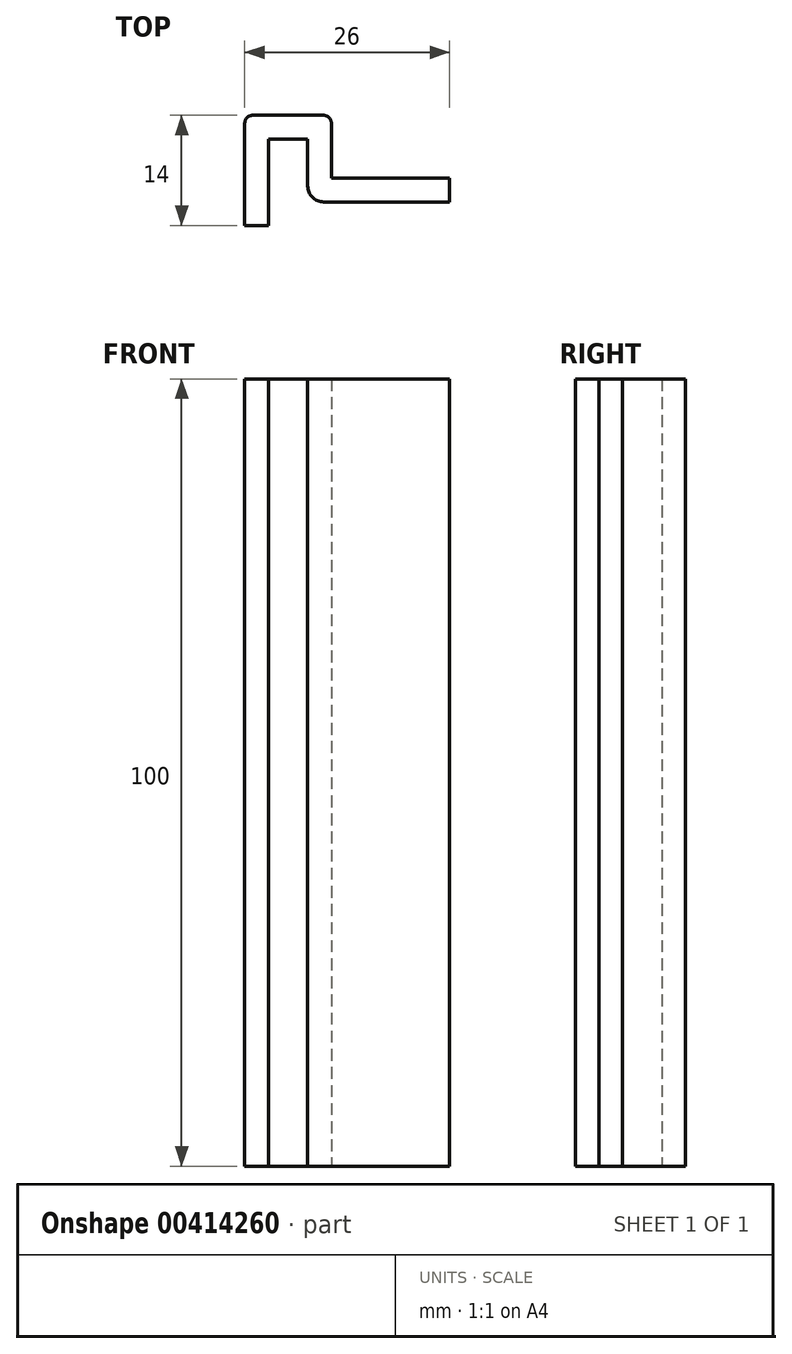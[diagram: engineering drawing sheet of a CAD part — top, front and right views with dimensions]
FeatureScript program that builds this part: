
annotation { "Feature Type Name" : "Feature", "Feature Type Description" : "" }
export const myFeature = defineFeature(function(context is Context, id is Id, definition is map)
    precondition{}
    {
        {
            var Q0;
            Q0=qCreatedBy(makeId("Top.planeOp"),FACE);
            var sketch = newSketch(context, id + "F0", { "sketchPlane" : qUnion([Q0])});
            skLineSegment(sketch, "E0", {"start": v(0, 0) * mm, "end": v(0, 14) * mm});
            skLineSegment(sketch, "E1", {"start": v(0, 14) * mm, "end": v(11, 14) * mm});
            skLineSegment(sketch, "E2", {"start": v(11, 14) * mm, "end": v(11, 6) * mm});
            skLineSegment(sketch, "E3", {"start": v(11, 6) * mm, "end": v(26, 6) * mm});
            skLineSegment(sketch, "E4", {"start": v(26, 6) * mm, "end": v(26, 3) * mm});
            skLineSegment(sketch, "E5", {"start": v(26, 3) * mm, "end": v(8, 3) * mm});
            skLineSegment(sketch, "E6", {"start": v(8, 3) * mm, "end": v(8, 11) * mm});
            skLineSegment(sketch, "E7", {"start": v(8, 11) * mm, "end": v(3, 11) * mm});
            skLineSegment(sketch, "E8", {"start": v(3, 11) * mm, "end": v(3, 0) * mm});
            skLineSegment(sketch, "E9", {"start": v(3, 0) * mm, "end": v(0, 0) * mm});
            skSolve(sketch);
        }
        {
            var Q0;
            Q0=qSketchRegion(id+"F0",true);
            extrude(context, id + "F1", {"entities" : qUnion([Q0]), "depth" : 100 * mm});
        }
        {
            var Q0;
            Q0=makeQuery(id+"F1.opExtrude","SWEPT_EDGE",EDGE,{"disambiguationData":[OSD([sQuery(id+"F0.wireOp",EDGE,"E5"),sQuery(id+"F0.wireOp",EDGE,"E6")])]});
            fillet(context, id + "F2", {"entities" : qUnion([Q0]), "radius" : 2 * mm, "tangentPropagation" : true, "allowEdgeOverflow" : false});
        }
        {
            var Q0;
            Q0=makeQuery(id+"F1.opExtrude","SWEPT_EDGE",EDGE,{"disambiguationData":[OSD([sQuery(id+"F0.wireOp",EDGE,"E0"),sQuery(id+"F0.wireOp",EDGE,"E1")])]});
            var Q1;
            Q1=makeQuery(id+"F1.opExtrude","SWEPT_EDGE",EDGE,{"disambiguationData":[OSD([sQuery(id+"F0.wireOp",EDGE,"E1"),sQuery(id+"F0.wireOp",EDGE,"E2")])]});
            fillet(context, id + "F3", {"entities" : qUnion([Q0, Q1]), "radius" : 1 * mm, "tangentPropagation" : true, "allowEdgeOverflow" : false});
        }
    });
